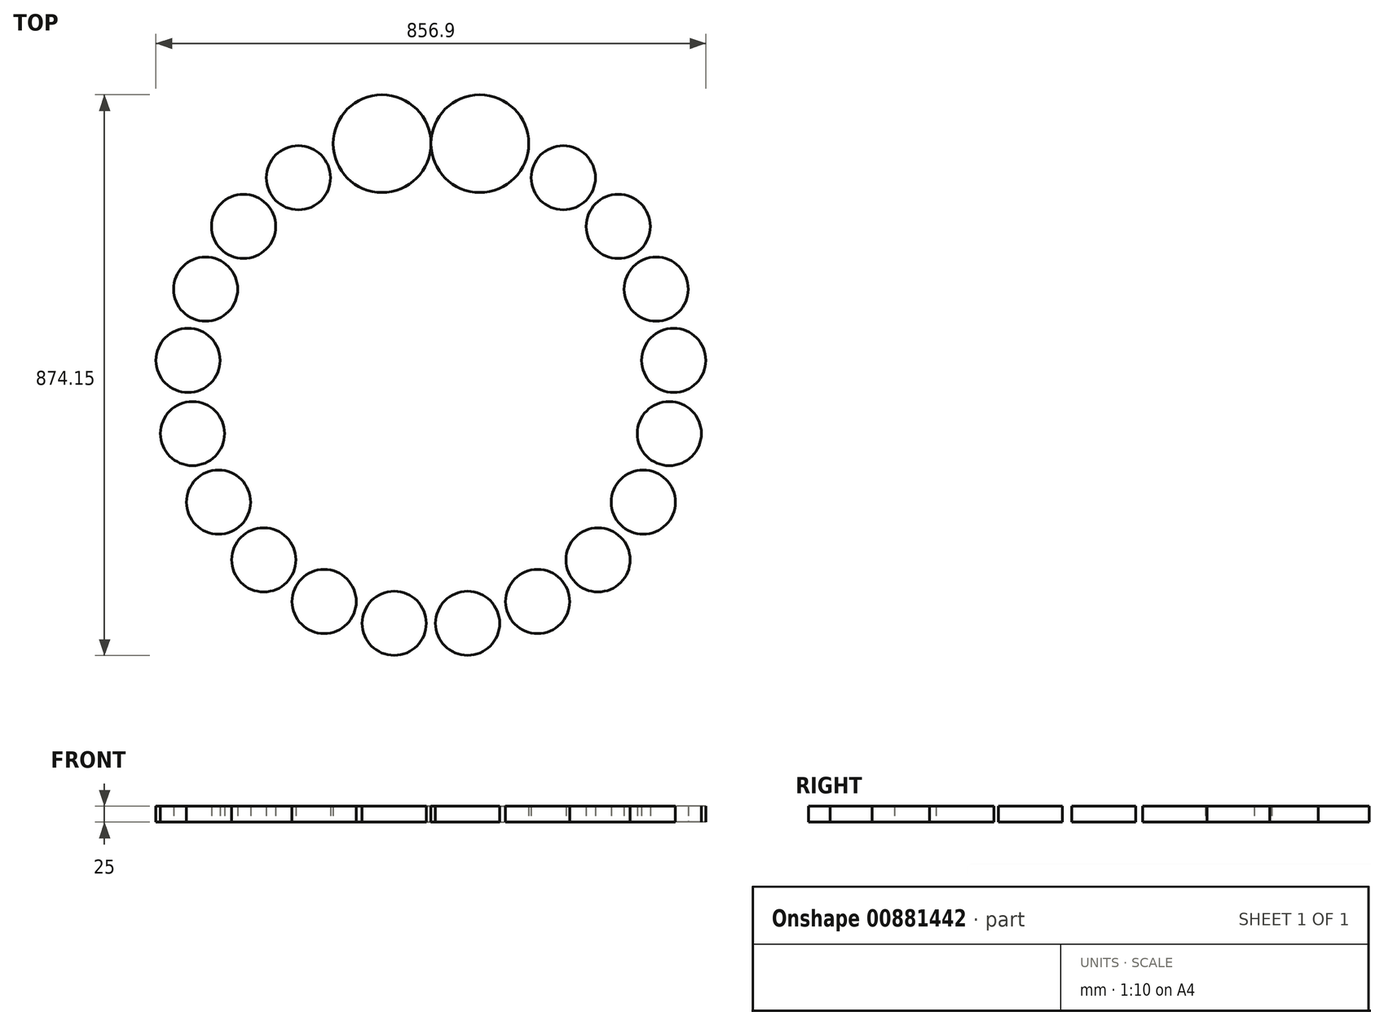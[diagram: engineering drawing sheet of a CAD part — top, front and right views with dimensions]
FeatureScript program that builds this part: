
annotation { "Feature Type Name" : "Feature", "Feature Type Description" : "" }
export const myFeature = defineFeature(function(context is Context, id is Id, definition is map)
    precondition{}
    {
        {
            var Q0;
            Q0=qCreatedBy(makeId("Top.planeOp"),FACE);
            var sketch = newSketch(context, id + "F0", { "sketchPlane" : qUnion([Q0])});
            skCircle(sketch, "E0", {"center": v(0, 0) * mm, "radius": 280 * mm, "construction": true});
            skCircle(sketch, "E1", {"center": v(0, 0) * mm, "radius": 380 * mm, "construction": true});
            skCircle(sketch, "E2", {"center": v(-76.2, 372.28) * mm, "radius": 76.2 * mm});
            skLineSegment(sketch, "E3", {"start": v(0, 0) * mm, "end": v(0, 666.18) * mm, "construction": true});
            skLineSegment(sketch, "E4", {"start": v(0, 0) * mm, "end": v(-261.75, 612.6) * mm, "construction": true});
            skCircle(sketch, "E5.MirrorC", {"center": v(76.2, 372.28) * mm, "radius": 76.2 * mm});
            skLineSegment(sketch, "E6.MirrorCS", {"start": v(0, 0) * mm, "end": v(261.75, 612.6) * mm, "construction": true});
            skCircle(sketch, "E7", {"center": v(-206.4, 319.07) * mm, "radius": 50 * mm});
            skCircle(sketch, "E8.1.0", {"center": v(-291.96, 243.22) * mm, "radius": 50 * mm});
            skCircle(sketch, "E8.2.0", {"center": v(-351.1, 145.36) * mm, "radius": 50 * mm});
            skCircle(sketch, "E8.3.0", {"center": v(-378.45, 34.34) * mm, "radius": 50 * mm});
            skCircle(sketch, "E8.4.0", {"center": v(-371.53, -79.8) * mm, "radius": 50 * mm});
            skCircle(sketch, "E8.5.0", {"center": v(-330.97, -186.7) * mm, "radius": 50 * mm});
            skCircle(sketch, "E8.6.0", {"center": v(-260.44, -276.71) * mm, "radius": 50 * mm});
            skCircle(sketch, "E8.7.0", {"center": v(-166.34, -341.66) * mm, "radius": 50 * mm});
            skCircle(sketch, "E8.8.0", {"center": v(-57.17, -375.67) * mm, "radius": 50 * mm});
            skCircle(sketch, "E8.9.0", {"center": v(57.17, -375.67) * mm, "radius": 50 * mm});
            skCircle(sketch, "E8.10.0", {"center": v(166.34, -341.66) * mm, "radius": 50 * mm});
            skCircle(sketch, "E8.11.0", {"center": v(260.44, -276.71) * mm, "radius": 50 * mm});
            skCircle(sketch, "E8.12.0", {"center": v(330.97, -186.7) * mm, "radius": 50 * mm});
            skCircle(sketch, "E8.13.0", {"center": v(371.53, -79.8) * mm, "radius": 50 * mm});
            skCircle(sketch, "E8.14.0", {"center": v(378.45, 34.34) * mm, "radius": 50 * mm});
            skCircle(sketch, "E8.15.0", {"center": v(351.1, 145.36) * mm, "radius": 50 * mm});
            skCircle(sketch, "E8.16.0", {"center": v(291.96, 243.22) * mm, "radius": 50 * mm});
            skCircle(sketch, "E8.17.0", {"center": v(206.4, 319.07) * mm, "radius": 50 * mm});
            skLineSegment(sketch, "E9", {"start": v(-206.4, 319.07) * mm, "end": v(-291.96, 243.22) * mm, "construction": true});
            skLineSegment(sketch, "E10", {"start": v(-291.96, 243.22) * mm, "end": v(-351.1, 145.36) * mm, "construction": true});
            skLineSegment(sketch, "E11", {"start": v(-351.1, 145.36) * mm, "end": v(-378.45, 34.34) * mm, "construction": true});
            skLineSegment(sketch, "E12", {"start": v(-378.45, 34.34) * mm, "end": v(-371.53, -79.8) * mm, "construction": true});
            skLineSegment(sketch, "E13", {"start": v(-371.53, -79.8) * mm, "end": v(-330.97, -186.7) * mm, "construction": true});
            skLineSegment(sketch, "E14", {"start": v(-330.97, -186.7) * mm, "end": v(-260.44, -276.71) * mm, "construction": true});
            skLineSegment(sketch, "E15", {"start": v(-260.44, -276.71) * mm, "end": v(-166.34, -341.66) * mm, "construction": true});
            skLineSegment(sketch, "E16", {"start": v(-166.34, -341.66) * mm, "end": v(-57.17, -375.67) * mm, "construction": true});
            skLineSegment(sketch, "E17", {"start": v(-57.17, -375.67) * mm, "end": v(57.17, -375.67) * mm, "construction": true});
            skLineSegment(sketch, "E18", {"start": v(57.17, -375.67) * mm, "end": v(166.34, -341.66) * mm, "construction": true});
            skLineSegment(sketch, "E19", {"start": v(166.34, -341.66) * mm, "end": v(260.44, -276.71) * mm, "construction": true});
            skLineSegment(sketch, "E20", {"start": v(260.44, -276.71) * mm, "end": v(330.97, -186.7) * mm, "construction": true});
            skLineSegment(sketch, "E21", {"start": v(330.97, -186.7) * mm, "end": v(371.53, -79.8) * mm, "construction": true});
            skLineSegment(sketch, "E22", {"start": v(371.53, -79.8) * mm, "end": v(378.45, 34.34) * mm, "construction": true});
            skLineSegment(sketch, "E23", {"start": v(378.45, 34.34) * mm, "end": v(351.1, 145.36) * mm, "construction": true});
            skLineSegment(sketch, "E24", {"start": v(291.96, 243.22) * mm, "end": v(351.1, 145.36) * mm, "construction": true});
            skLineSegment(sketch, "E25", {"start": v(291.96, 243.22) * mm, "end": v(206.4, 319.07) * mm, "construction": true});
            skPoint(sketch, "E26", {"position": v(-149.3, 349.44) * mm});
            skPoint(sketch, "E27", {"position": v(149.3, 349.44) * mm});
            skCircle(sketch, "E28", {"center": v(-102.13, 366.02) * mm, "radius": 50 * mm, "construction": true});
            skCircle(sketch, "E29.MirrorC", {"center": v(102.13, 366.02) * mm, "radius": 50 * mm, "construction": true});
            skLineSegment(sketch, "E30", {"start": v(-206.4, 319.07) * mm, "end": v(-102.13, 366.02) * mm, "construction": true});
            skLineSegment(sketch, "E31", {"start": v(102.13, 366.02) * mm, "end": v(206.4, 319.07) * mm, "construction": true});
            skSolve(sketch);
        }
        {
            var Q0;
            Q0 = qSketchRegion(id + "F0", true);
            extrude(context, id + "F1", {"entities" : qUnion([Q0]), "depth" : 25 * mm, "offsetDistance" : 25 * mm});
        }
    });
